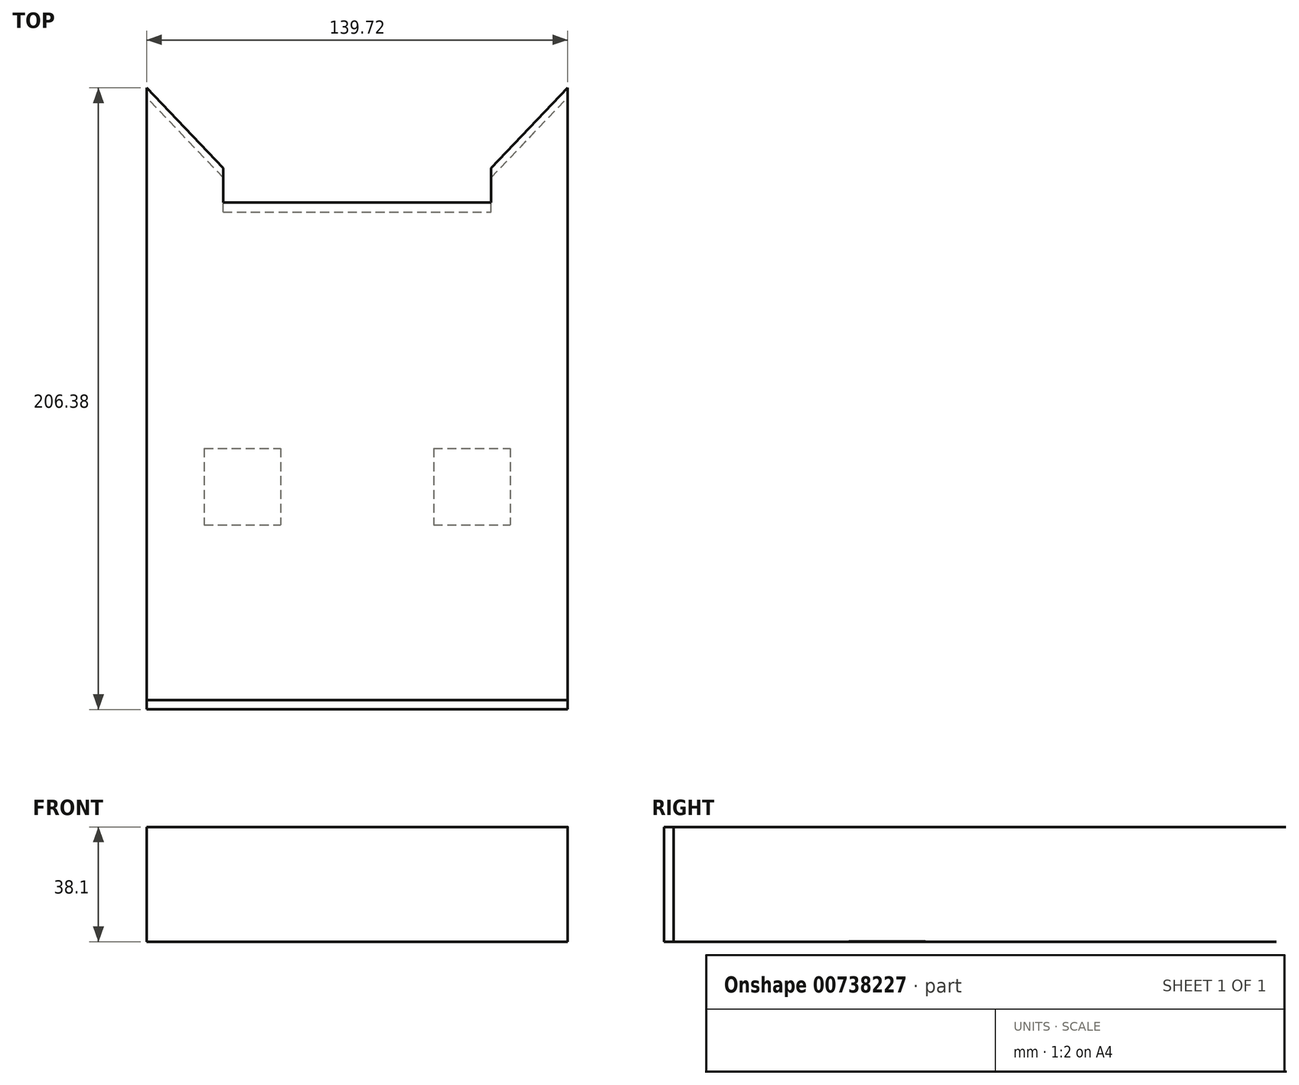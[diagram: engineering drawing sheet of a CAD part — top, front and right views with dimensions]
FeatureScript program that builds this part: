
annotation { "Feature Type Name" : "Feature", "Feature Type Description" : "" }
export const myFeature = defineFeature(function(context is Context, id is Id, definition is map)
    precondition{}
    {
        {
            var Q0;
            Q0=qCreatedBy(makeId("Top.planeOp"),FACE);
            var sketch = newSketch(context, id + "F0", { "sketchPlane" : qUnion([Q0])});
            skLineSegment(sketch, "E0.bottom", {"start": v(-54, 124.18) * mm, "end": v(85.7, 124.18) * mm});
            skLineSegment(sketch, "E0.top", {"start": v(-54, -79.02) * mm, "end": v(85.7, -79.02) * mm});
            skLineSegment(sketch, "E0.left", {"start": v(-54, 124.18) * mm, "end": v(-54, -79.02) * mm});
            skLineSegment(sketch, "E0.right", {"start": v(85.7, 124.18) * mm, "end": v(85.7, -79.02) * mm});
            skSolve(sketch);
        }
        {
            var Q0;
            Q0=makeQuery(id+"F0.imprint","IMPRINT",FACE,{"disambiguationData":[TD([[makeQuery(id+"F0.imprint","IMPRINT",EDGE,{"derivedFrom":sQuery(id+"F0.wireOp",EDGE,"E0.bottom")}),-1.0]])]});
            extrude(context, id + "F1", {"entities" : qUnion([Q0]), "oppositeDirection" : true, "depth" : 1 / 203.2 * mm, "offsetDistance" : 25.4 * mm});
        }
        {
            var Q0;
            Q0=makeQuery(id+"F1.opExtrude","CAP_FACE",FACE,{"disambiguationData":[OSD([sQuery(id+"F0.wireOp",EDGE,"E0.bottom"),sQuery(id+"F0.wireOp",EDGE,"E0.top"),sQuery(id+"F0.wireOp",EDGE,"E0.left"),sQuery(id+"F0.wireOp",EDGE,"E0.right")])],"isStart":true});
            var sketch = newSketch(context, id + "F2", { "sketchPlane" : qUnion([Q0])});
            skLineSegment(sketch, "E1", {"start": v(-54, 86.08) * mm, "end": v(85.7, 86.08) * mm});
            skLineSegment(sketch, "E2", {"start": v(-28.6, 86.08) * mm, "end": v(-28.6, 97.51) * mm});
            skLineSegment(sketch, "E3", {"start": v(-28.6, 97.51) * mm, "end": v(-54, 124.18) * mm});
            skLineSegment(sketch, "E4", {"start": v(60.3, 86.08) * mm, "end": v(60.3, 97.51) * mm});
            skLineSegment(sketch, "E5", {"start": v(60.3, 97.51) * mm, "end": v(85.7, 124.18) * mm});
            skSolve(sketch);
        }
        {
            var Q0;
            {var subQ1=sQuery(id+"F2.wireOp",EDGE,"E2");Q0=makeQuery(id+"F2.imprint","IMPRINT",FACE,{"disambiguationData":[TD([[makeQuery(id+"F2.imprint","IMPRINT",EDGE,{"derivedFrom":subQ1}),-1.0]])]});}
            extrude(context, id + "F3", {"entities" : qUnion([Q0]), "operationType" : NewBodyOperationType.REMOVE, "oppositeDirection" : true, "depth" : 1 / 203.2 * mm, "offsetDistance" : 25.4 * mm});
        }
        {
            var Q0;
            Q0=makeQuery(id+"F1.opExtrude","CAP_FACE",FACE,{"disambiguationData":[OSD([sQuery(id+"F0.wireOp",EDGE,"E0.bottom"),sQuery(id+"F0.wireOp",EDGE,"E0.top"),sQuery(id+"F0.wireOp",EDGE,"E0.left"),sQuery(id+"F0.wireOp",EDGE,"E0.right")])],"isStart":true});
            var sketch = newSketch(context, id + "F4", { "sketchPlane" : qUnion([Q0])});
            skLineSegment(sketch, "E6.bottom", {"start": v(-34.93, 7.68) * mm, "end": v(-9.53, 7.68) * mm});
            skLineSegment(sketch, "E6.top", {"start": v(-34.93, -17.72) * mm, "end": v(-9.53, -17.72) * mm});
            skLineSegment(sketch, "E6.left", {"start": v(-34.93, 7.68) * mm, "end": v(-34.93, -17.72) * mm});
            skLineSegment(sketch, "E6.right", {"start": v(-9.53, 7.68) * mm, "end": v(-9.53, -17.72) * mm});
            skLineSegment(sketch, "E7.bottom", {"start": v(41.22, 7.68) * mm, "end": v(66.62, 7.68) * mm});
            skLineSegment(sketch, "E7.top", {"start": v(41.22, -17.72) * mm, "end": v(66.62, -17.72) * mm});
            skLineSegment(sketch, "E7.left", {"start": v(41.22, 7.68) * mm, "end": v(41.22, -17.72) * mm});
            skLineSegment(sketch, "E7.right", {"start": v(66.62, 7.68) * mm, "end": v(66.62, -17.72) * mm});
            skSolve(sketch);
        }
        {
            var Q0;
            Q0 = qSketchRegion(id + "F4", true);
            var Q1;
            Q1 = qSketchRegion(id + "F8", true);
            extrude(context, id + "F5", {"entities" : qUnion([Q0, Q1]), "operationType" : NewBodyOperationType.ADD, "depth" : 1 / 50.8 * mm, "offsetDistance" : 25.4 * mm});
        }
        {
            var Q0;
            Q0=makeQuery(id+"F1.opExtrude","CAP_FACE",FACE,{"disambiguationData":[OSD([sQuery(id+"F0.wireOp",EDGE,"E0.bottom"),sQuery(id+"F0.wireOp",EDGE,"E0.top"),sQuery(id+"F0.wireOp",EDGE,"E0.left"),sQuery(id+"F0.wireOp",EDGE,"E0.right")])],"isStart":true});
            var sketch = newSketch(context, id + "F6", { "sketchPlane" : qUnion([Q0])});
            skLineSegment(sketch, "E8.bottom", {"start": v(85.7, -79.02) * mm, "end": v(-54, -79.02) * mm});
            skLineSegment(sketch, "E8.top", {"start": v(85.7, -75.84) * mm, "end": v(-54, -75.84) * mm});
            skLineSegment(sketch, "E8.left", {"start": v(85.7, -79.02) * mm, "end": v(85.7, -75.84) * mm});
            skLineSegment(sketch, "E8.right", {"start": v(-54, -79.02) * mm, "end": v(-54, -75.84) * mm});
            skSolve(sketch);
        }
        {
            var Q0;
            Q0=makeQuery(id+"F6.imprint","IMPRINT",FACE,{"disambiguationData":[TD([[makeQuery(id+"F6.imprint","IMPRINT",EDGE,{"derivedFrom":sQuery(id+"F6.wireOp",EDGE,"E8.bottom")}),1.0]])]});
            extrude(context, id + "F7", {"entities" : qUnion([Q0]), "depth" : 38.1 * mm, "offsetDistance" : 25.4 * mm});
        }
        {
            var Q0;
            Q0=makeQuery(id+"F7.opExtrude","CAP_FACE",FACE,{"disambiguationData":[OSD([sQuery(id+"F6.wireOp",EDGE,"E8.bottom"),sQuery(id+"F6.wireOp",EDGE,"E8.top"),sQuery(id+"F6.wireOp",EDGE,"E8.left"),sQuery(id+"F6.wireOp",EDGE,"E8.right")])],"isStart":false});
            var sketch = newSketch(context, id + "F8", { "sketchPlane" : qUnion([Q0])});
            skLineSegment(sketch, "E9.bottom", {"start": v(-54, -75.84) * mm, "end": v(85.72, -75.84) * mm});
            skLineSegment(sketch, "E9.top", {"start": v(-54, 127.36) * mm, "end": v(85.72, 127.36) * mm});
            skLineSegment(sketch, "E9.left", {"start": v(-54, -75.84) * mm, "end": v(-54, 127.36) * mm});
            skLineSegment(sketch, "E9.right", {"start": v(85.72, -75.84) * mm, "end": v(85.72, 127.36) * mm});
            skSolve(sketch);
        }
        {
            var Q0;
            Q0 = qSketchRegion(id + "F8", true);
            extrude(context, id + "F9", {"entities" : qUnion([Q0]), "depth" : 1 / 203.2 * mm, "offsetDistance" : 25.4 * mm});
        }
        {
            var Q0;
            Q0=makeQuery(id+"F9.opExtrude","CAP_FACE",FACE,{"disambiguationData":[OSD([sQuery(id+"F8.wireOp",EDGE,"E9.bottom"),sQuery(id+"F8.wireOp",EDGE,"E9.top"),sQuery(id+"F8.wireOp",EDGE,"E9.left"),sQuery(id+"F8.wireOp",EDGE,"E9.right")])],"isStart":false});
            var sketch = newSketch(context, id + "F10", { "sketchPlane" : qUnion([Q0])});
            skLineSegment(sketch, "E10", {"start": v(-54, 89.26) * mm, "end": v(85.72, 89.26) * mm});
            skLineSegment(sketch, "E11", {"start": v(-28.6, 89.26) * mm, "end": v(-28.6, 100.69) * mm});
            skLineSegment(sketch, "E12", {"start": v(60.32, 89.26) * mm, "end": v(60.32, 100.69) * mm});
            skLineSegment(sketch, "E13", {"start": v(-28.6, 100.69) * mm, "end": v(-54, 127.36) * mm});
            skLineSegment(sketch, "E14", {"start": v(60.32, 100.69) * mm, "end": v(85.72, 127.36) * mm});
            skSolve(sketch);
        }
        {
            var Q0;
            Q0 = qSketchRegion(id + "F10", true);
            var Q1;
            {var subQ1=sQuery(id+"F10.wireOp",EDGE,"E11");Q1=makeQuery(id+"F10.imprint","IMPRINT",FACE,{"disambiguationData":[TD([[makeQuery(id+"F10.imprint","IMPRINT",EDGE,{"derivedFrom":subQ1}),-1.0]])]});}
            extrude(context, id + "F11", {"entities" : qUnion([Q0, Q1]), "operationType" : NewBodyOperationType.REMOVE, "oppositeDirection" : true, "depth" : 25.4 * mm, "offsetDistance" : 25.4 * mm});
        }
        {
            var Q0;
            Q0=makeQuery(id+"F9.opExtrude","SWEPT_FACE",FACE,{"disambiguationData":[OSD([sQuery(id+"F8.wireOp",EDGE,"E9.bottom")])]});
            extrude(context, id + "F12", {"entities" : qUnion([Q0]), "operationType" : NewBodyOperationType.ADD, "depth" : 1 / 203.2 * mm, "offsetDistance" : 25.4 * mm});
        }
    });
